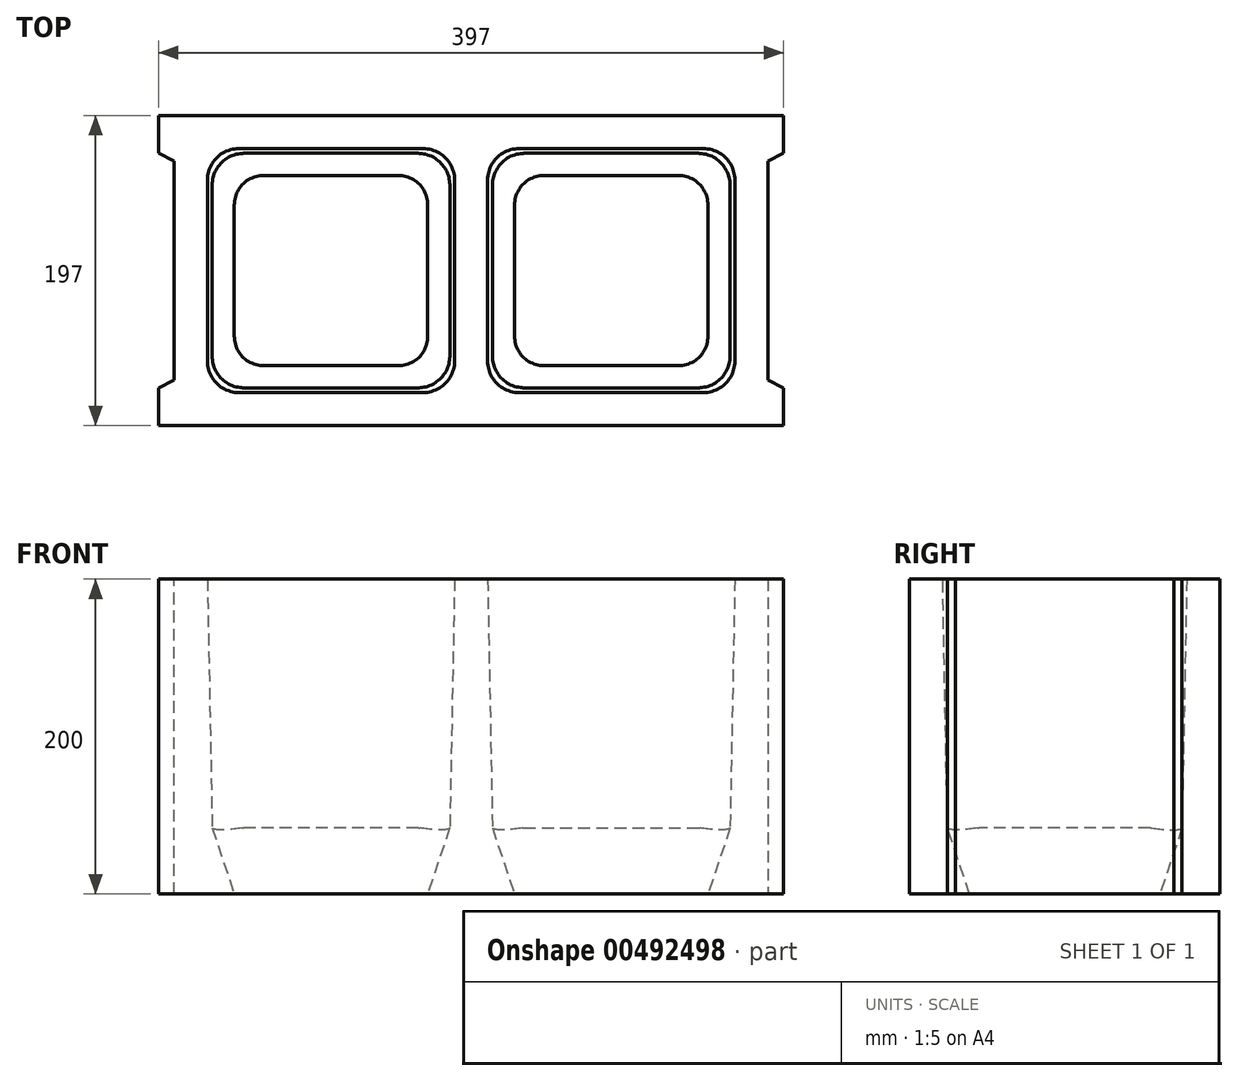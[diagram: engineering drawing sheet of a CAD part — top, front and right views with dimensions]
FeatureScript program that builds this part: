
annotation { "Feature Type Name" : "Feature", "Feature Type Description" : "" }
export const myFeature = defineFeature(function(context is Context, id is Id, definition is map)
    precondition{}
    {
        {
            var Q0;
            Q0=qCreatedBy(makeId("Top.planeOp"),FACE);
            var sketch = newSketch(context, id + "F0", { "sketchPlane" : qUnion([Q0])});
            skLineSegment(sketch, "E0.bottom", {"start": v(-198.5, 98.5) * mm, "end": v(0, 98.5) * mm});
            skLineSegment(sketch, "E0.top", {"start": v(-198.5, -98.5) * mm, "end": v(0, -98.5) * mm});
            skLineSegment(sketch, "E0.left", {"start": v(-198.5, 98.5) * mm, "end": v(-198.5, -98.5) * mm});
            skLineSegment(sketch, "E0.right", {"start": v(0, 98.5) * mm, "end": v(0, -98.5) * mm});
            skSolve(sketch);
        }
        {
            var Q0;
            Q0 = qSketchRegion(id + "F0", true);
            extrude(context, id + "F1", {"entities" : qUnion([Q0]), "depth" : 200 * mm});
        }
        {
            var Q0;
            Q0=makeQuery(id+"F1.opExtrude","CAP_FACE",FACE,{"disambiguationData":[OSD([sQuery(id+"F0.wireOp",EDGE,"E0.bottom"),sQuery(id+"F0.wireOp",EDGE,"E0.top"),sQuery(id+"F0.wireOp",EDGE,"E0.left"),sQuery(id+"F0.wireOp",EDGE,"E0.right")])],"isStart":false});
            var sketch = newSketch(context, id + "F2", { "sketchPlane" : qUnion([Q0])});
            skLineSegment(sketch, "E1.bottom", {"start": v(-167.5, 77.5) * mm, "end": v(-10.5, 77.5) * mm});
            skLineSegment(sketch, "E1.top", {"start": v(-167.5, -77.5) * mm, "end": v(-10.5, -77.5) * mm});
            skLineSegment(sketch, "E1.left", {"start": v(-167.5, 77.5) * mm, "end": v(-167.5, -77.5) * mm});
            skLineSegment(sketch, "E1.right", {"start": v(-10.5, 77.5) * mm, "end": v(-10.5, -77.5) * mm});
            skSolve(sketch);
        }
        {
            var Q0;
            Q0=makeQuery(id+"F2.imprint","IMPRINT",FACE,{"disambiguationData":[TD([[makeQuery(id+"F2.imprint","IMPRINT",EDGE,{"derivedFrom":sQuery(id+"F2.wireOp",EDGE,"E1.bottom")}),-1.0]])]});
            extrude(context, id + "F3", {"entities" : qUnion([Q0]), "operationType" : NewBodyOperationType.REMOVE, "oppositeDirection" : true, "depth" : 158 * mm, "hasDraft" : true, "draftAngle" : 1.1 * degree, "draftPullDirection" : true});
        }
        {
            var Q0;
            Q0=makeQuery(id+"F3.boolean.opBoolean","COPY",FACE,{"derivedFrom":makeQuery(id+"F3.opExtrude","CAP_FACE",FACE,{"disambiguationData":[OSD([sQuery(id+"F2.wireOp",EDGE,"E1.bottom"),sQuery(id+"F2.wireOp",EDGE,"E1.top"),sQuery(id+"F2.wireOp",EDGE,"E1.left"),sQuery(id+"F2.wireOp",EDGE,"E1.right")])],"isStart":false})});
            extrude(context, id + "F4", {"entities" : qUnion([Q0]), "operationType" : NewBodyOperationType.REMOVE, "endBound" : BoundingType.THROUGH_ALL, "oppositeDirection" : true, "depth" : 25 * mm, "hasDraft" : true, "draftAngle" : 18.5 * degree, "draftPullDirection" : true});
        }
        {
            var Q0;
            Q0=makeQuery(id+"F1.opExtrude","CAP_FACE",FACE,{"disambiguationData":[OSD([sQuery(id+"F0.wireOp",EDGE,"E0.bottom"),sQuery(id+"F0.wireOp",EDGE,"E0.top"),sQuery(id+"F0.wireOp",EDGE,"E0.left"),sQuery(id+"F0.wireOp",EDGE,"E0.right")])],"isStart":false});
            var sketch = newSketch(context, id + "F5", { "sketchPlane" : qUnion([Q0])});
            skLineSegment(sketch, "E2.bottom", {"start": v(-198.5, 74.5) * mm, "end": v(-188.5, 74.5) * mm});
            skLineSegment(sketch, "E2.top", {"start": v(-198.5, -74.5) * mm, "end": v(-188.5, -74.5) * mm});
            skLineSegment(sketch, "E2.left", {"start": v(-198.5, 74.5) * mm, "end": v(-198.5, -74.5) * mm});
            skLineSegment(sketch, "E2.right", {"start": v(-188.5, 74.5) * mm, "end": v(-188.5, -74.5) * mm});
            skSolve(sketch);
        }
        {
            var Q0;
            Q0=makeQuery(id+"F5.imprint","IMPRINT",FACE,{"disambiguationData":[TD([[makeQuery(id+"F5.imprint","IMPRINT",EDGE,{"derivedFrom":sQuery(id+"F5.wireOp",EDGE,"E2.bottom")}),-1.0]])]});
            extrude(context, id + "F6", {"entities" : qUnion([Q0]), "operationType" : NewBodyOperationType.REMOVE, "endBound" : BoundingType.THROUGH_ALL, "oppositeDirection" : true, "depth" : 25 * mm});
        }
        {
            var Q0;
            Q0=makeQuery(id+"F1.opExtrude","SWEPT_BODY",BODY,{"disambiguationData":[OSD([sQuery(id+"F0.wireOp",EDGE,"E0.bottom"),sQuery(id+"F0.wireOp",EDGE,"E0.top"),sQuery(id+"F0.wireOp",EDGE,"E0.left"),sQuery(id+"F0.wireOp",EDGE,"E0.right")])]});
            var Q1;
            Q1=qCreatedBy(makeId("Right.planeOp"),FACE);
            mirror(context, id + "F7", {"operationType" : NewBodyOperationType.ADD, "entities" : qUnion([Q0]), "mirrorPlane" : qUnion([Q1])});
        }
        {
            var Q0;
            Q0=makeQuery(id+"F7.opPattern","COPY",EDGE,{"derivedFrom":makeQuery(id+"F3.boolean.opBoolean","COPY",EDGE,{"derivedFrom":makeQuery(id+"F3.opExtrude","SWEPT_EDGE",EDGE,{"disambiguationData":[OSD([sQuery(id+"F2.wireOp",EDGE,"E1.top"),sQuery(id+"F2.wireOp",EDGE,"E1.left")])]})}),"instanceName":"1"});
            var Q1;
            Q1=makeQuery(id+"F7.opPattern","COPY",EDGE,{"derivedFrom":makeQuery(id+"F4.boolean.opBoolean","COPY",EDGE,{"derivedFrom":makeQuery(id+"F4.opExtrude","SWEPT_EDGE",EDGE,{"disambiguationData":[OSD([sQuery(id+"F2.wireOp",EDGE,"E1.top"),sQuery(id+"F2.wireOp",EDGE,"E1.left")])]})}),"instanceName":"1"});
            var Q2;
            Q2=makeQuery(id+"F3.boolean.opBoolean","COPY",EDGE,{"derivedFrom":makeQuery(id+"F3.opExtrude","SWEPT_EDGE",EDGE,{"disambiguationData":[OSD([sQuery(id+"F2.wireOp",EDGE,"E1.top"),sQuery(id+"F2.wireOp",EDGE,"E1.right")])]})});
            var Q3;
            Q3=makeQuery(id+"F4.boolean.opBoolean","COPY",EDGE,{"derivedFrom":makeQuery(id+"F4.opExtrude","SWEPT_EDGE",EDGE,{"disambiguationData":[OSD([sQuery(id+"F2.wireOp",EDGE,"E1.top"),sQuery(id+"F2.wireOp",EDGE,"E1.right")])]})});
            fillet(context, id + "F8", {"entities" : qUnion([Q0, Q1, Q2, Q3]), "radius" : 20 * mm, "tangentPropagation" : true, "allowEdgeOverflow" : false});
        }
        {
            var Q0;
            Q0=makeQuery(id+"F7.opPattern","COPY",EDGE,{"derivedFrom":makeQuery(id+"F3.boolean.opBoolean","COPY",EDGE,{"derivedFrom":makeQuery(id+"F3.opExtrude","SWEPT_EDGE",EDGE,{"disambiguationData":[OSD([sQuery(id+"F2.wireOp",EDGE,"E1.top"),sQuery(id+"F2.wireOp",EDGE,"E1.right")])]})}),"instanceName":"1"});
            var Q1;
            Q1=makeQuery(id+"F7.opPattern","COPY",EDGE,{"derivedFrom":makeQuery(id+"F4.boolean.opBoolean","COPY",EDGE,{"derivedFrom":makeQuery(id+"F4.opExtrude","SWEPT_EDGE",EDGE,{"disambiguationData":[OSD([sQuery(id+"F2.wireOp",EDGE,"E1.top"),sQuery(id+"F2.wireOp",EDGE,"E1.right")])]})}),"instanceName":"1"});
            var Q2;
            Q2=makeQuery(id+"F3.boolean.opBoolean","COPY",EDGE,{"derivedFrom":makeQuery(id+"F3.opExtrude","SWEPT_EDGE",EDGE,{"disambiguationData":[OSD([sQuery(id+"F2.wireOp",EDGE,"E1.top"),sQuery(id+"F2.wireOp",EDGE,"E1.left")])]})});
            var Q3;
            Q3=makeQuery(id+"F4.boolean.opBoolean","COPY",EDGE,{"derivedFrom":makeQuery(id+"F4.opExtrude","SWEPT_EDGE",EDGE,{"disambiguationData":[OSD([sQuery(id+"F2.wireOp",EDGE,"E1.top"),sQuery(id+"F2.wireOp",EDGE,"E1.left")])]})});
            fillet(context, id + "F9", {"entities" : qUnion([Q0, Q1, Q2, Q3]), "radius" : 20 * mm, "tangentPropagation" : true, "allowEdgeOverflow" : false});
        }
        {
            var Q0;
            Q0=makeQuery(id+"F3.boolean.opBoolean","COPY",EDGE,{"derivedFrom":makeQuery(id+"F3.opExtrude","SWEPT_EDGE",EDGE,{"disambiguationData":[OSD([sQuery(id+"F2.wireOp",EDGE,"E1.bottom"),sQuery(id+"F2.wireOp",EDGE,"E1.left")])]})});
            var Q1;
            Q1=makeQuery(id+"F4.boolean.opBoolean","COPY",EDGE,{"derivedFrom":makeQuery(id+"F4.opExtrude","SWEPT_EDGE",EDGE,{"disambiguationData":[OSD([sQuery(id+"F2.wireOp",EDGE,"E1.bottom"),sQuery(id+"F2.wireOp",EDGE,"E1.left")])]})});
            fillet(context, id + "F10", {"entities" : qUnion([Q0, Q1]), "radius" : 20 * mm, "tangentPropagation" : true, "allowEdgeOverflow" : false});
        }
        {
            var Q0;
            Q0=makeQuery(id+"F7.opPattern","COPY",EDGE,{"derivedFrom":makeQuery(id+"F3.boolean.opBoolean","COPY",EDGE,{"derivedFrom":makeQuery(id+"F3.opExtrude","SWEPT_EDGE",EDGE,{"disambiguationData":[OSD([sQuery(id+"F2.wireOp",EDGE,"E1.bottom"),sQuery(id+"F2.wireOp",EDGE,"E1.right")])]})}),"instanceName":"1"});
            var Q1;
            Q1=makeQuery(id+"F7.opPattern","COPY",EDGE,{"derivedFrom":makeQuery(id+"F4.boolean.opBoolean","COPY",EDGE,{"derivedFrom":makeQuery(id+"F4.opExtrude","SWEPT_EDGE",EDGE,{"disambiguationData":[OSD([sQuery(id+"F2.wireOp",EDGE,"E1.bottom"),sQuery(id+"F2.wireOp",EDGE,"E1.right")])]})}),"instanceName":"1"});
            fillet(context, id + "F11", {"entities" : qUnion([Q0, Q1]), "radius" : 20 * mm, "tangentPropagation" : true, "allowEdgeOverflow" : false});
        }
        {
            var Q0;
            Q0=makeQuery(id+"F3.boolean.opBoolean","COPY",EDGE,{"derivedFrom":makeQuery(id+"F3.opExtrude","SWEPT_EDGE",EDGE,{"disambiguationData":[OSD([sQuery(id+"F2.wireOp",EDGE,"E1.bottom"),sQuery(id+"F2.wireOp",EDGE,"E1.right")])]})});
            var Q1;
            Q1=makeQuery(id+"F4.boolean.opBoolean","COPY",EDGE,{"derivedFrom":makeQuery(id+"F4.opExtrude","SWEPT_EDGE",EDGE,{"disambiguationData":[OSD([sQuery(id+"F2.wireOp",EDGE,"E1.bottom"),sQuery(id+"F2.wireOp",EDGE,"E1.right")])]})});
            var Q2;
            Q2=makeQuery(id+"F7.opPattern","COPY",EDGE,{"derivedFrom":makeQuery(id+"F3.boolean.opBoolean","COPY",EDGE,{"derivedFrom":makeQuery(id+"F3.opExtrude","SWEPT_EDGE",EDGE,{"disambiguationData":[OSD([sQuery(id+"F2.wireOp",EDGE,"E1.bottom"),sQuery(id+"F2.wireOp",EDGE,"E1.left")])]})}),"instanceName":"1"});
            var Q3;
            Q3=makeQuery(id+"F7.opPattern","COPY",EDGE,{"derivedFrom":makeQuery(id+"F4.boolean.opBoolean","COPY",EDGE,{"derivedFrom":makeQuery(id+"F4.opExtrude","SWEPT_EDGE",EDGE,{"disambiguationData":[OSD([sQuery(id+"F2.wireOp",EDGE,"E1.bottom"),sQuery(id+"F2.wireOp",EDGE,"E1.left")])]})}),"instanceName":"1"});
            fillet(context, id + "F12", {"entities" : qUnion([Q0, Q1, Q2, Q3]), "radius" : 20 * mm, "tangentPropagation" : true, "allowEdgeOverflow" : false});
        }
        {
            var Q0;
            Q0=makeQuery(id+"F7.opPattern","COPY",EDGE,{"derivedFrom":makeQuery(id+"F6.boolean.opBoolean","COPY",EDGE,{"derivedFrom":makeQuery(id+"F6.opExtrude","SWEPT_EDGE",EDGE,{"disambiguationData":[OSD([sQuery(id+"F5.wireOp",EDGE,"E2.bottom"),sQuery(id+"F5.wireOp",EDGE,"E2.right")])]})}),"instanceName":"1"});
            var Q1;
            Q1=makeQuery(id+"F7.opPattern","COPY",EDGE,{"derivedFrom":makeQuery(id+"F6.boolean.opBoolean","COPY",EDGE,{"derivedFrom":makeQuery(id+"F6.opExtrude","SWEPT_EDGE",EDGE,{"disambiguationData":[OSD([sQuery(id+"F5.wireOp",EDGE,"E2.top"),sQuery(id+"F5.wireOp",EDGE,"E2.right")])]})}),"instanceName":"1"});
            chamfer(context, id + "F13", {"entities" : qUnion([Q0, Q1]), "chamferType" : ChamferType.TWO_OFFSETS, "width1" : 5 * mm, "oppositeDirection" : false, "width2" : 10 * mm, "tangentPropagation" : true});
        }
        {
            var Q0;
            Q0=makeQuery(id+"F6.boolean.opBoolean","COPY",EDGE,{"derivedFrom":makeQuery(id+"F6.opExtrude","SWEPT_EDGE",EDGE,{"disambiguationData":[OSD([sQuery(id+"F5.wireOp",EDGE,"E2.bottom"),sQuery(id+"F5.wireOp",EDGE,"E2.right")])]})});
            var Q1;
            Q1=makeQuery(id+"F6.boolean.opBoolean","COPY",EDGE,{"derivedFrom":makeQuery(id+"F6.opExtrude","SWEPT_EDGE",EDGE,{"disambiguationData":[OSD([sQuery(id+"F5.wireOp",EDGE,"E2.top"),sQuery(id+"F5.wireOp",EDGE,"E2.right")])]})});
            chamfer(context, id + "F14", {"entities" : qUnion([Q0, Q1]), "chamferType" : ChamferType.TWO_OFFSETS, "width1" : 10 * mm, "oppositeDirection" : false, "width2" : 5 * mm, "tangentPropagation" : true});
        }
        {
            var Q0;
            Q0=makeQuery(id+"F1.opExtrude","SWEPT_BODY",BODY,{"disambiguationData":[OSD([sQuery(id+"F0.wireOp",EDGE,"E0.bottom"),sQuery(id+"F0.wireOp",EDGE,"E0.top"),sQuery(id+"F0.wireOp",EDGE,"E0.left"),sQuery(id+"F0.wireOp",EDGE,"E0.right")])]});
            transform(context, id + "F15", {"entities" : qUnion([Q0]), "transformType" : TransformType.TRANSLATION_3D, "dx" : 0 * mm, "dy" : 0 * mm, "dz" : 0 * mm, "makeCopy" : true});
        }
        {
            var Q0;
            Q0=makeQuery(id+"F15.opPattern","COPY",BODY,{"derivedFrom":makeQuery(id+"F1.opExtrude","SWEPT_BODY",BODY,{"disambiguationData":[OSD([sQuery(id+"F0.wireOp",EDGE,"E0.bottom"),sQuery(id+"F0.wireOp",EDGE,"E0.top"),sQuery(id+"F0.wireOp",EDGE,"E0.left"),sQuery(id+"F0.wireOp",EDGE,"E0.right")])]}),"instanceName":"1"});
            deleteBodies(context, id + "F16", {"entities" : qUnion([Q0])});
        }
    });
